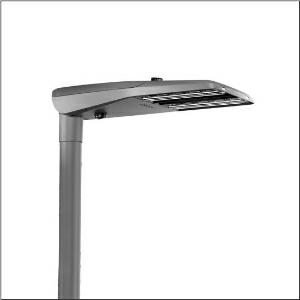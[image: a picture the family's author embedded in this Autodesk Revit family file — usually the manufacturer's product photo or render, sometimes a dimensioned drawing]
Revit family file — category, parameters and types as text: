
# Revit family: streetlight_sl_11_iq_midi___pc-r_5xc3f51y08me_63e7
name_source: partatom
category: Lighting Fixtures
units: mm (PartAtom-declared; Revit-internal decimal feet)

## family parameters
Cut with Voids When Loaded = No
Host = Face
Light Source = No
Part Type = Normal
Room Calculation Point = No
Round Connector Dimension = Use Diameter
Shared = No

## types (1)
- --- (1 x LED, 15540 lm, 122.7 W, 3000K)
    Apparent Load = 123 VA
    CIE Flux Codes = 37 73 96 100 100
    Color Rendering = 70
    Color Temperature = 3000K
    Default Elevation = 1800 mm
    Description = Streetlight SL 11 iQ midi, mast luminaire, primary light control with 3 zone facetted reflector, of plastic, silver coated, highly specular, primary optical cover: cover, of PMMA, transparent, light distribution: PC-R, light emission: direct distribution, primary light characteristic: asymmetric, right, installation type: post-top, side-entry, lamps: LED, High Power LED, rated values: 15.540lm | 122,7W | 126,7lm/W (begin service life); end service life: 15.540lm | 130,2W; at 50% lumin. flux: 7.770lm | 56,1W | 138,5lm/W, colour temperature: 3000K, colour rendering: CRI > 70, light colour: 730, light setting 1 begin service life: 100% | 15.540lm | 122,7W | 126,7lm/W | 3.000K, light setting 1 end service life: 130,2W, further light settings possible, control: pre-setting: logarithmic dimming characteristic, Street-Remote, Auto-Match, Temp-Guard, Lumen-Switch, Night-Set, Smart-Wire, Light-Fading, Desk-Remote (wireless, voltage-free reading and setting of iQ features in the workshop via application-optimized NFC function/RFID function), optimised constant luminous flux control (CLO 2.0), with cable H07RN-F 5x 1.5mm², mains connection: 230..240V, AC, 50/60Hz, connection cable pre-assembled, cable length: 12,5m, luminaire housing, of diecast aluminium, powder-coated, Siteco® metallic grey (DB 702S), please order mast flange separately, inclination adjustable without tools: 0°, 5°, 10°, 15° (post-top) | 0°, -5°, -10°, -15° (side-entry), sealing non-destructively replaceable, multi-level sealing system, length: 780mm, width: 376mm, height: 118mm, mast flange for spigot size: 42mm (side-entry): 5XC10008XM4, 60/48mm (side-entry/post-top): 5XC10108XM2, 76/60mm (side-entry/post-top): 5XC10108XM1, equipment: Power, Smart Interface below and above, protection rating (complete): IP66, insulation class (complete): insulation class II (safety insulation), certification: CE, ENEC, ENEC+, VDE, UKCA, impact resistance: IK10, permissible operating ambient temperature for outdoor applications: -25..+50°C, standard-compliant lighting for roads and squares, Environmental Product Declaration (EPD) tested and certified by an independent institute, packaging unit: 1 piece

Light Distribution: PC-R
    Height = 118 mm
    Lamp = 1 x LED
    Lamp Light Flux = 15540 lm
    Lamp Power = 122.7 W
    Lamp count = 1
    Length = 780 mm
    Luminous efficacy = 127 lm/W
    Manufacturer = Siteco
    ModVariant = No
    Model = 5XC3F51Y08ME
    Number of Poles = 1
    OnlyDefault = Yes
    Power Factor = 1
    Product Name = Streetlight SL 11 iQ midi | PC-R
    Product group = mast luminaire | pylon top
    ProductGroupID = 6100
    Protection Class = Protection class II
    Protection Degree = IP 66
    RLX_Detail_Level = 1
    RLX_Emergency_Light_Flux = 0 lm
    RLX_Emergency_Type = 0
    RLX_Emergency_Type_DB = No
    RlxData = <blob elided: 73737 chars, md5=d6900df7>
    Socket = socket
    Standby Power = 0 W
    System Light Flux = 15540 lm
    System Power = 123 W
    Type Comments = factory setting: luminous flux: 100 % | dim-lin: 254 | 552 mA
    Type Image = l_1004429.jpg
    URL = http://relux.com
    VarID = @adj_154441
    Voltage = 0 V
    Weight = 0.00 kg
    Width = 376 mm

## geometry (parser evidence)
native form markers: Blend x4, Sweep x9
no freeform markers — native parametric forms only
